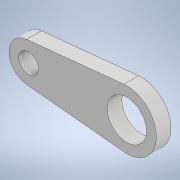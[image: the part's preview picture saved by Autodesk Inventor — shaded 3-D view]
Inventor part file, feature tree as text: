
AUTODESK INVENTOR PART (.ipt)
format: ipt  version: 2022 (Build 260153000, 153)  size: 114,688 bytes
history: native  units: mm
features: other x1, extrude x1, sketch x1
ambient origin geometry x8: Origin, YZ Plane, XZ Plane, XY Plane, X Axis, Y Axis, Z Axis, Center Point
bodies: Body1 (feature_tree)
feature tree (3):
  other  "Sólido1"
  extrude  "Extrusão1"  Depth=15.0mm
  sketch  "Esboço1"  dims[d0=20.0mm d1=40.0mm d2=40.0mm d3=60.0mm d4=100.0mm d5=0.0mm d6=0.0mm d7=15.0mm d8=0.0mm]
